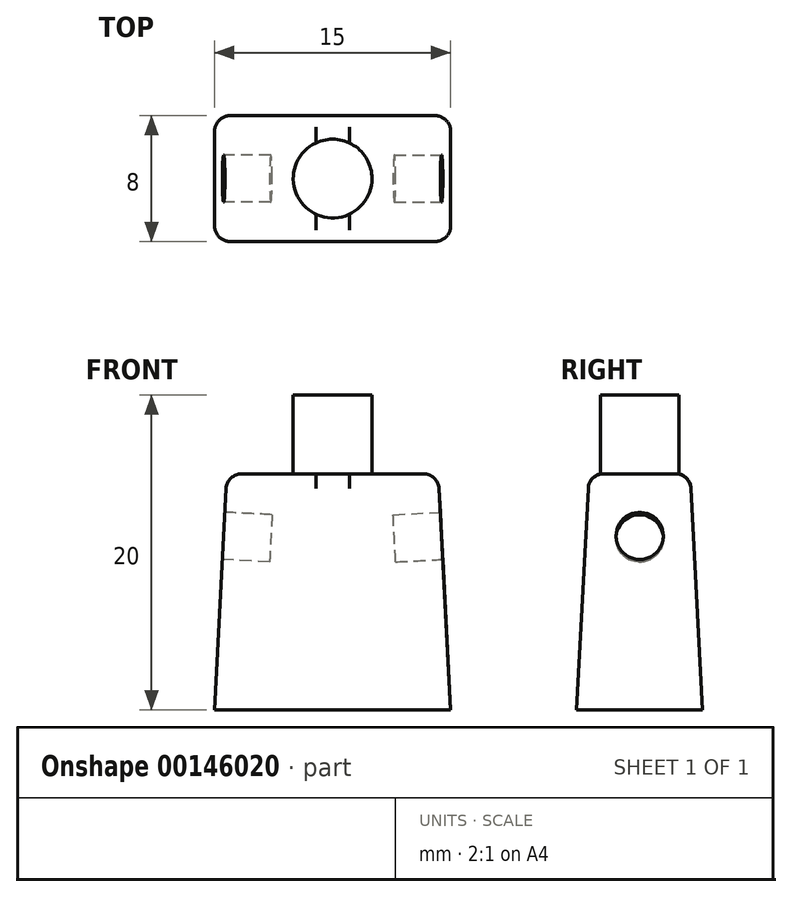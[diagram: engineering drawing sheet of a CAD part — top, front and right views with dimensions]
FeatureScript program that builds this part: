
annotation { "Feature Type Name" : "Feature", "Feature Type Description" : "" }
export const myFeature = defineFeature(function(context is Context, id is Id, definition is map)
    precondition{}
    {
        {
            var Q0;
            Q0=qCreatedBy(makeId("Top.planeOp"),FACE);
            var sketch = newSketch(context, id + "F0", { "sketchPlane" : qUnion([Q0])});
            skLineSegment(sketch, "E0.bottom", {"start": v(7.5, -4) * mm, "end": v(-7.5, -4) * mm});
            skLineSegment(sketch, "E0.top", {"start": v(7.5, 4) * mm, "end": v(-7.5, 4) * mm});
            skLineSegment(sketch, "E0.left", {"start": v(7.5, -4) * mm, "end": v(7.5, 4) * mm});
            skLineSegment(sketch, "E0.right", {"start": v(-7.5, -4) * mm, "end": v(-7.5, 4) * mm});
            skPoint(sketch, "E0.middle", {"position": v(0, 0) * mm});
            skSolve(sketch);
        }
        {
            var Q0;
            Q0=qSketchRegion(id+"F0",true);
            extrude(context, id + "F1", {"entities" : qUnion([Q0]), "depth" : 15 * mm, "hasDraft" : true, "draftAngle" : 3 * degree, "draftPullDirection" : true});
        }
        {
            var Q0;
            Q0=makeQuery(id+"F1.opExtrude","CAP_FACE",FACE,{"disambiguationData":[OSD([sQuery(id+"F0.wireOp",EDGE,"E0.bottom"),sQuery(id+"F0.wireOp",EDGE,"E0.top"),sQuery(id+"F0.wireOp",EDGE,"E0.left"),sQuery(id+"F0.wireOp",EDGE,"E0.right")])],"isStart":false});
            var sketch = newSketch(context, id + "F2", { "sketchPlane" : qUnion([Q0])});
            skCircle(sketch, "E1", {"center": v(0, 0) * mm, "radius": 2.5 * mm});
            skSolve(sketch);
        }
        {
            var Q0;
            Q0=qSketchRegion(id+"F2",true);
            extrude(context, id + "F3", {"entities" : qUnion([Q0]), "operationType" : NewBodyOperationType.ADD, "depth" : 5 * mm});
        }
        {
            var Q0;
            Q0=makeQuery(id+"F1.opExtrude","SWEPT_EDGE",EDGE,{"disambiguationData":[OSD([sQuery(id+"F0.wireOp",EDGE,"E0.bottom"),sQuery(id+"F0.wireOp",EDGE,"E0.left")])]});
            var Q1;
            Q1=makeQuery(id+"F1.opExtrude","SWEPT_EDGE",EDGE,{"disambiguationData":[OSD([sQuery(id+"F0.wireOp",EDGE,"E0.top"),sQuery(id+"F0.wireOp",EDGE,"E0.left")])]});
            var Q2;
            Q2=makeQuery(id+"F1.opExtrude","CAP_EDGE",EDGE,{"disambiguationData":[OSD([sQuery(id+"F0.wireOp",EDGE,"E0.top")])],"isStart":false});
            var Q3;
            Q3=makeQuery(id+"F1.opExtrude","CAP_EDGE",EDGE,{"disambiguationData":[OSD([sQuery(id+"F0.wireOp",EDGE,"E0.left")])],"isStart":false});
            var Q4;
            Q4=makeQuery(id+"F1.opExtrude","CAP_EDGE",EDGE,{"disambiguationData":[OSD([sQuery(id+"F0.wireOp",EDGE,"E0.bottom")])],"isStart":false});
            var Q5;
            Q5=makeQuery(id+"F1.opExtrude","CAP_EDGE",EDGE,{"disambiguationData":[OSD([sQuery(id+"F0.wireOp",EDGE,"E0.right")])],"isStart":false});
            var Q6;
            Q6=makeQuery(id+"F1.opExtrude","SWEPT_EDGE",EDGE,{"disambiguationData":[OSD([sQuery(id+"F0.wireOp",EDGE,"E0.bottom"),sQuery(id+"F0.wireOp",EDGE,"E0.right")])]});
            var Q7;
            Q7=makeQuery(id+"F1.opExtrude","SWEPT_EDGE",EDGE,{"disambiguationData":[OSD([sQuery(id+"F0.wireOp",EDGE,"E0.top"),sQuery(id+"F0.wireOp",EDGE,"E0.right")])]});
            fillet(context, id + "F4", {"entities" : qUnion([Q0, Q1, Q2, Q3, Q4, Q5, Q6, Q7]), "radius" : 1 * mm, "tangentPropagation" : true, "allowEdgeOverflow" : false});
        }
        {
            var Q0;
            Q0=makeQuery(id+"F1.opExtrude","SWEPT_FACE",FACE,{"disambiguationData":[OSD([sQuery(id+"F0.wireOp",EDGE,"E0.left")])]});
            var sketch = newSketch(context, id + "F5", { "sketchPlane" : qUnion([Q0])});
            skSolve(sketch);
        }
        {
            var Q0;
            Q0=qCreatedBy(makeId("Right.planeOp"),FACE);
            var sketch = newSketch(context, id + "F6", { "sketchPlane" : qUnion([Q0])});
            skCircle(sketch, "E2", {"center": v(0, 11.05) * mm, "radius": 1.5 * mm});
            skSolve(sketch);
        }
        {
            var Q0;
            Q0=qSketchRegion(id+"F6",true);
            extrude(context, id + "F7", {"entities" : qUnion([Q0]), "operationType" : NewBodyOperationType.ADD, "endBound" : BoundingType.SYMMETRIC, "depth" : 3 * mm});
        }
        {
            var Q0;
            Q0=makeQuery(id+"F1.opExtrude","SWEPT_FACE",FACE,{"disambiguationData":[OSD([sQuery(id+"F0.wireOp",EDGE,"E0.right")])]});
            var sketch = newSketch(context, id + "F8", { "sketchPlane" : qUnion([Q0])});
            skCircle(sketch, "E3", {"center": v(0, 10.68) * mm, "radius": 1.5 * mm});
            skSolve(sketch);
        }
        {
            var Q0;
            Q0=qSketchRegion(id+"F8",true);
            extrude(context, id + "F9", {"entities" : qUnion([Q0]), "operationType" : NewBodyOperationType.REMOVE, "oppositeDirection" : true, "depth" : 3 * mm});
        }
        {
            var Q0;
            {var subQ0=sQuery(id+"F0.wireOp",EDGE,"E0.left");Q0=makeQuery(id+"F5.imprint","IMPRINT",FACE,{"disambiguationData":[TD([[makeQuery(id+"F5.imprint","IMPRINT",EDGE,{"derivedFrom":makeQuery(id+"F1.opExtrude","CAP_EDGE",EDGE,{"disambiguationData":[OSD([subQ0])],"isStart":true})}),1.0]])]});}
            var sketch = newSketch(context, id + "F10", { "sketchPlane" : qUnion([Q0])});
            skCircle(sketch, "E4", {"center": v(0, 10.68) * mm, "radius": 1.5 * mm});
            skSolve(sketch);
        }
        {
            var Q0;
            Q0=qSketchRegion(id+"F10",true);
            extrude(context, id + "F11", {"entities" : qUnion([Q0]), "operationType" : NewBodyOperationType.REMOVE, "oppositeDirection" : true, "depth" : 3 * mm});
        }
    });
